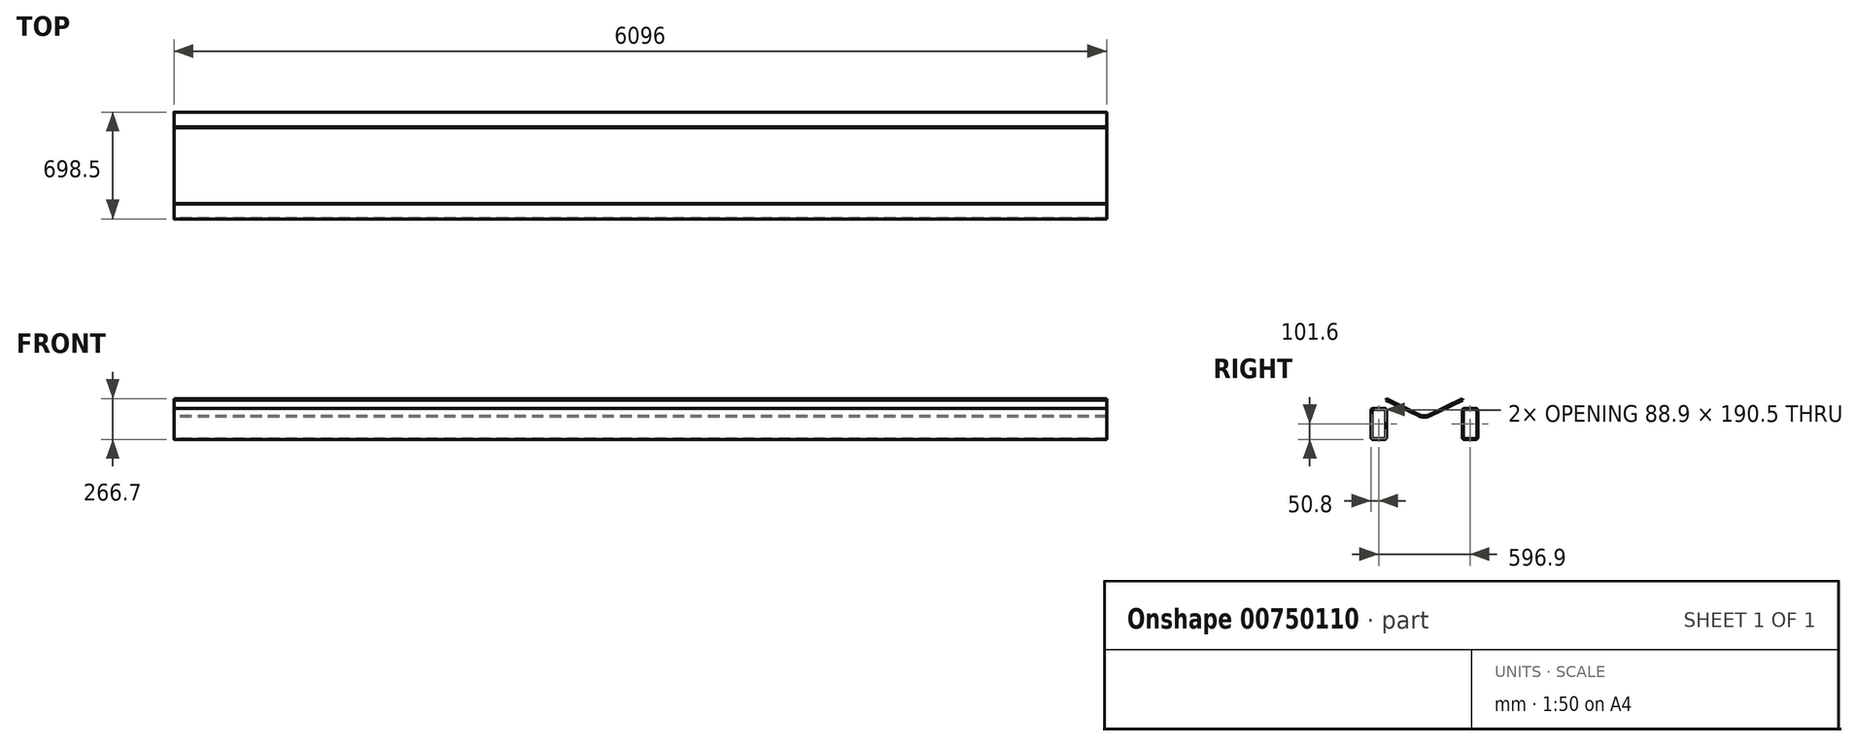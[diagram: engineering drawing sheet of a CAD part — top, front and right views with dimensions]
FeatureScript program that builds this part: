
annotation { "Feature Type Name" : "Feature", "Feature Type Description" : "" }
export const myFeature = defineFeature(function(context is Context, id is Id, definition is map)
    precondition{}
    {
        {
            var Q0;
            Q0=qCreatedBy(makeId("Right.planeOp"),FACE);
            var sketch = newSketch(context, id + "F0", { "sketchPlane" : qUnion([Q0])});
            skPoint(sketch, "E0", {"position": v(0, 0) * mm});
            skLineSegment(sketch, "E1", {"start": v(0, 228.65) * mm, "end": v(0, -305.7) * mm, "construction": true});
            skLineSegment(sketch, "E2.bottom", {"start": v(-336.55, 57.15) * mm, "end": v(-260.35, 57.15) * mm});
            skLineSegment(sketch, "E2.top", {"start": v(-336.55, -146.05) * mm, "end": v(-260.35, -146.05) * mm});
            skLineSegment(sketch, "E2.left", {"start": v(-349.25, 44.45) * mm, "end": v(-349.25, -133.35) * mm});
            skLineSegment(sketch, "E2.right", {"start": v(-247.65, 44.45) * mm, "end": v(-247.65, -133.35) * mm});
            skPoint(sketch, "E3.visualSharp", {"position": v(-247.65, 57.15) * mm});
            skArc(sketch, "E3.filletArc", {"start": v(-247.65, 44.45) * mm, "mid": v(-251.37, 53.43) * mm, "end": v(-260.35, 57.15) * mm});
            skPoint(sketch, "E4.visualSharp", {"position": v(-349.25, -146.05) * mm});
            skArc(sketch, "E4.filletArc", {"start": v(-349.25, -133.35) * mm, "mid": v(-345.53, -142.33) * mm, "end": v(-336.55, -146.05) * mm});
            skPoint(sketch, "E5.visualSharp", {"position": v(-247.65, -146.05) * mm});
            skArc(sketch, "E5.filletArc", {"start": v(-260.35, -146.05) * mm, "mid": v(-251.37, -142.33) * mm, "end": v(-247.65, -133.35) * mm});
            skPoint(sketch, "E6.visualSharp", {"position": v(-349.25, 57.15) * mm});
            skArc(sketch, "E6.filletArc", {"start": v(-336.55, 57.15) * mm, "mid": v(-345.53, 53.43) * mm, "end": v(-349.25, 44.45) * mm});
            skLineSegment(sketch, "E7.MirrorCS", {"start": v(247.65, 44.45) * mm, "end": v(247.65, -133.35) * mm});
            skArc(sketch, "E8.MirrorCS", {"start": v(247.65, 44.45) * mm, "mid": v(251.37, 53.43) * mm, "end": v(260.35, 57.15) * mm});
            skLineSegment(sketch, "E9.MirrorCS", {"start": v(336.55, 57.15) * mm, "end": v(260.35, 57.15) * mm});
            skArc(sketch, "E10.MirrorCS", {"start": v(336.55, 57.15) * mm, "mid": v(345.53, 53.43) * mm, "end": v(349.25, 44.45) * mm});
            skLineSegment(sketch, "E11.MirrorCS", {"start": v(349.25, 44.45) * mm, "end": v(349.25, -133.35) * mm});
            skArc(sketch, "E12.MirrorCS", {"start": v(349.25, -133.35) * mm, "mid": v(345.53, -142.33) * mm, "end": v(336.55, -146.05) * mm});
            skLineSegment(sketch, "E13.MirrorCS", {"start": v(336.55, -146.05) * mm, "end": v(260.35, -146.05) * mm});
            skPoint(sketch, "E14.MirrorP", {"position": v(247.65, -146.05) * mm});
            skArc(sketch, "E15.MirrorCS", {"start": v(260.35, -146.05) * mm, "mid": v(251.37, -142.33) * mm, "end": v(247.65, -133.35) * mm});
            skPoint(sketch, "E16.MirrorP", {"position": v(247.65, 57.15) * mm});
            skLineSegment(sketch, "E17", {"start": v(-247.65, 120.65) * mm, "end": v(-33.37, 16.26) * mm});
            skLineSegment(sketch, "E18.MirrorCS", {"start": v(247.65, 120.65) * mm, "end": v(33.37, 16.26) * mm});
            skLineSegment(sketch, "E19", {"start": v(-364.25, 120.65) * mm, "end": v(0, 120.65) * mm, "construction": true});
            skCircle(sketch, "E20", {"center": v(0, 211.9) * mm, "radius": 190.5 * mm, "construction": true});
            skArc(sketch, "E21.filletArc", {"start": v(-33.37, 16.26) * mm, "mid": v(0, 8.56) * mm, "end": v(33.37, 16.26) * mm});
            skCircle(sketch, "E22", {"center": v(0, 113.02) * mm, "radius": 101.6 * mm, "construction": true});
            skCircle(sketch, "E23", {"center": v(0, 59.33) * mm, "radius": 50.8 * mm, "construction": true});
            skArc(sketch, "E24.0", {"start": v(-336.55, 50.8) * mm, "mid": v(-341.04, 48.94) * mm, "end": v(-342.9, 44.45) * mm});
            skLineSegment(sketch, "E24.1", {"start": v(-342.9, 44.45) * mm, "end": v(-342.9, -133.35) * mm});
            skLineSegment(sketch, "E24.2", {"start": v(-336.55, 50.8) * mm, "end": v(-260.35, 50.8) * mm});
            skArc(sketch, "E24.3", {"start": v(-342.9, -133.35) * mm, "mid": v(-341.04, -137.84) * mm, "end": v(-336.55, -139.7) * mm});
            skArc(sketch, "E24.4", {"start": v(-254, 44.45) * mm, "mid": v(-255.86, 48.94) * mm, "end": v(-260.35, 50.8) * mm});
            skLineSegment(sketch, "E24.5", {"start": v(-254, 44.45) * mm, "end": v(-254, -133.35) * mm});
            skArc(sketch, "E24.6", {"start": v(-260.35, -139.7) * mm, "mid": v(-255.86, -137.84) * mm, "end": v(-254, -133.35) * mm});
            skLineSegment(sketch, "E24.7", {"start": v(-336.55, -139.7) * mm, "end": v(-260.35, -139.7) * mm});
            skArc(sketch, "E25.0", {"start": v(336.55, 50.8) * mm, "mid": v(341.04, 48.94) * mm, "end": v(342.9, 44.45) * mm});
            skLineSegment(sketch, "E25.1", {"start": v(342.9, 44.45) * mm, "end": v(342.9, -133.35) * mm});
            skLineSegment(sketch, "E25.2", {"start": v(336.55, 50.8) * mm, "end": v(260.35, 50.8) * mm});
            skArc(sketch, "E25.3", {"start": v(342.9, -133.35) * mm, "mid": v(341.04, -137.84) * mm, "end": v(336.55, -139.7) * mm});
            skArc(sketch, "E25.4", {"start": v(254, 44.45) * mm, "mid": v(255.86, 48.94) * mm, "end": v(260.35, 50.8) * mm});
            skLineSegment(sketch, "E25.5", {"start": v(254, 44.45) * mm, "end": v(254, -133.35) * mm});
            skArc(sketch, "E25.6", {"start": v(260.35, -139.7) * mm, "mid": v(255.86, -137.84) * mm, "end": v(254, -133.35) * mm});
            skLineSegment(sketch, "E25.7", {"start": v(336.55, -139.7) * mm, "end": v(260.35, -139.7) * mm});
            skLineSegment(sketch, "E26.0", {"start": v(251.82, 112.09) * mm, "end": v(37.54, 7.7) * mm});
            skArc(sketch, "E26.1", {"start": v(-37.54, 7.7) * mm, "mid": v(0, -0.96) * mm, "end": v(37.54, 7.7) * mm});
            skLineSegment(sketch, "E26.2", {"start": v(-251.78, 112.07) * mm, "end": v(-37.54, 7.7) * mm});
            skLineSegment(sketch, "E27", {"start": v(-247.65, 120.65) * mm, "end": v(-251.78, 112.07) * mm});
            skLineSegment(sketch, "E28", {"start": v(247.65, 120.65) * mm, "end": v(251.82, 112.09) * mm});
            skSolve(sketch);
        }
        {
            var Q0;
            Q0 = qSketchRegion(id + "F0", true);
            extrude(context, id + "F1", {"entities" : qUnion([Q0]), "depth" : 6096 * mm, "offsetDistance" : 25.4 * mm});
        }
    });
